# Revit family: Plumbing_Valves_Leonard-Valve_PNV-125-LF-Proton-Digital-Mixing-Valve
name_source: partatom
category: Pipe Accessories
revit_build: Autodesk Revit 2015 (Build: 20160512_1515(x64)
units: mm (PartAtom-declared; Revit-internal decimal feet)

## types (1)
- PNV-125-LF
    BIMobject category = Valves
    BIMobject category code = plumbing-valves
    BIMobject main category = Plumbing
    BIMobject main category code = plumbing
    Brand url = http://www.leonardvalve.com
    Cold Inlet Temperature Range = 39º - 80ºF
    Description = Leonard’s Newest, Sleek Digital Temperature Control Valve
    Design country = United States
    Edition number = 1
    Hot Inlet Temperature Range = 120º - 180ºF
    IFC Classification = Valve
    Inlet = 1"
    Installation instructions = http://www.leonardvalve.com
    Manufacturer = Leonard Valve
    Manufacturer country = United States
    Manufacturer name = Leonard Valve Company
    Masterformat 2014 Code = 23 09 13.33
    Masterformat 2014 Description = Control Valves
    Maximum Flow Rate = 120 GPM
    Maximum Pressure Drop = 50.00 psi
    Minimum Flow Rate = 0 GPM
    Model = PNV-125-LF
    NBS Reference Code = 94-94
    NBS Reference Description = Valves
    Nominal height = 0' - 0"
    Nominal width = 0' - 0"
    OmniClass Code = 23-27 31 29
    OmniClass Description = Mixing Valves
    Outlet = 1 1/2"
    Outlet Temperature Range = 65º - 180ºF
    Piping Method = Method W
    Product Guid = cb3322b5-28c3-4de2-b08c-f05be7862a5d
    Product SKU = pnv-125-Lf
    Product certification = http://www.leonardvalve.com
    Product data url = https://bimobject.com
    Product family = Mixing Valves for Liquid Services
    Product group = Digitally Controlled Mixing Valves
    Product url = http://www.leonardvalve.com
    QR code = http://bimobject.com
    Technical description = http://www.leonardvalve.com
    UNSPSC Code = 401416
    URL = http://www.leonardvalve.com
    Uniclass 1.4 Code = L71177
    Uniclass 1.4 Description = Mixing valves
    Uniclass 2.0 Code = PR-94
    Uniclass 2.0 Description = Valves
    Uniclass 2015 Code = Pr_65_54_40_16
    Uniclass 2015 Name = Control valves
    Uniformat II Code = D20
    Uniformat II Description = PLUMBING
    Water Pressure Maximum = 200.00 psi
    Weight Net (Kg) = 0

## geometry (parser evidence)
native form markers: Blend x2, Sweep x3
no freeform markers — native parametric forms only
